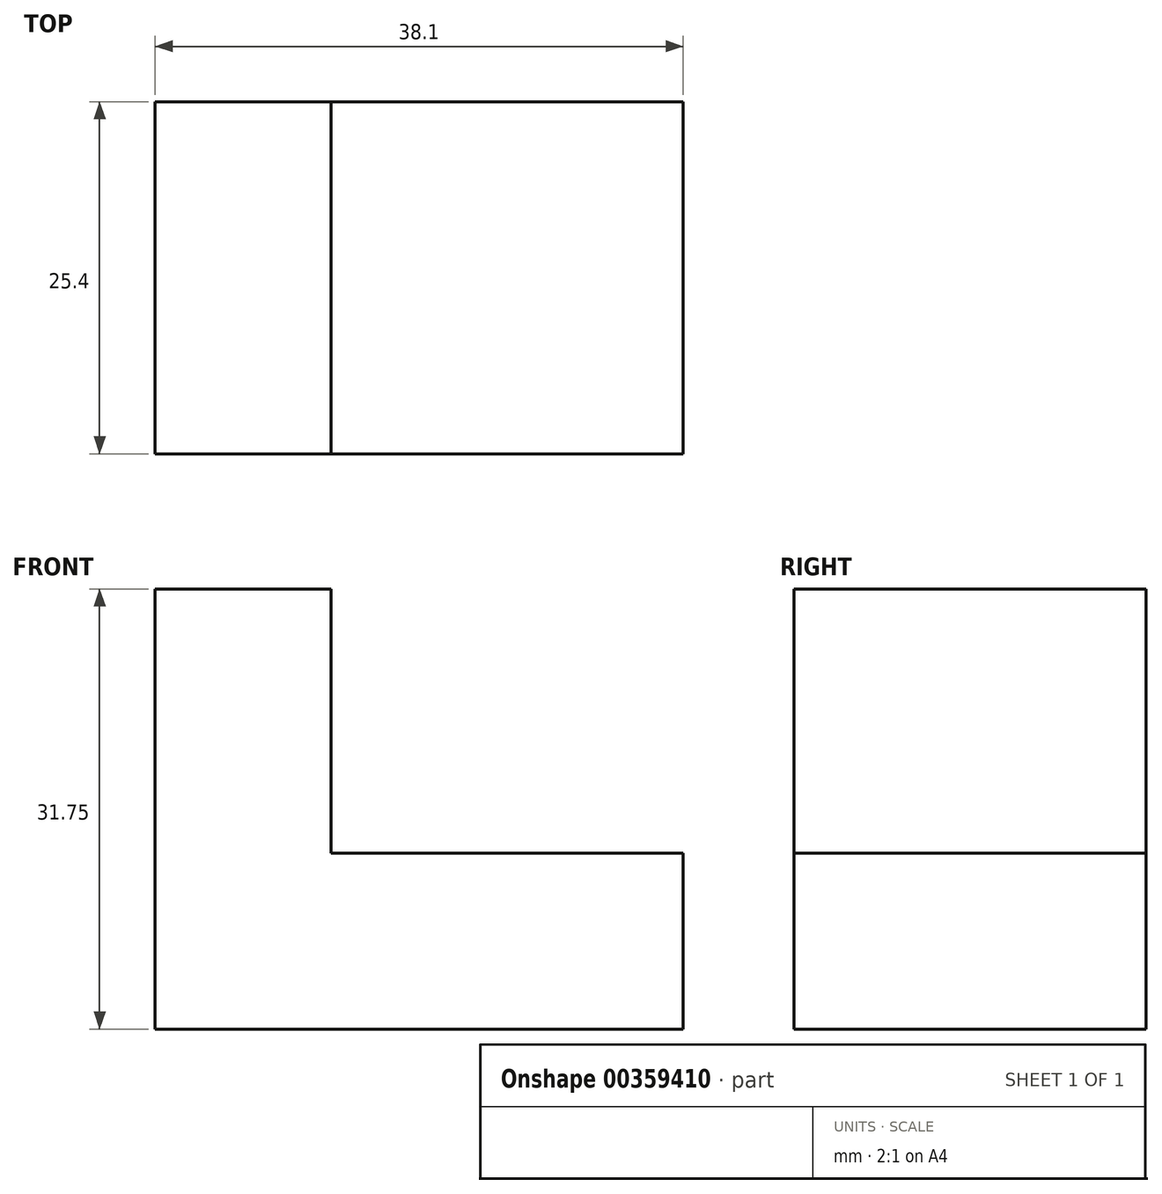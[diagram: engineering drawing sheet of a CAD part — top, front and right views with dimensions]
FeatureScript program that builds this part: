
annotation { "Feature Type Name" : "Feature", "Feature Type Description" : "" }
export const myFeature = defineFeature(function(context is Context, id is Id, definition is map)
    precondition{}
    {
        {
            var Q0;
            Q0=qCreatedBy(makeId("Front.planeOp"),FACE);
            var sketch = newSketch(context, id + "F0", { "sketchPlane" : qUnion([Q0])});
            skLineSegment(sketch, "E0", {"start": v(0, 31.75) * mm, "end": v(0, 0) * mm});
            skLineSegment(sketch, "E1", {"start": v(0, 0) * mm, "end": v(38.1, 0) * mm});
            skLineSegment(sketch, "E2", {"start": v(38.1, 0) * mm, "end": v(38.1, 12.7) * mm});
            skLineSegment(sketch, "E3", {"start": v(38.1, 12.7) * mm, "end": v(12.7, 12.7) * mm});
            skLineSegment(sketch, "E4", {"start": v(12.7, 12.7) * mm, "end": v(12.7, 31.75) * mm});
            skLineSegment(sketch, "E5", {"start": v(0, 31.75) * mm, "end": v(12.7, 31.75) * mm});
            skSolve(sketch);
        }
        {
            var Q0;
            Q0=makeQuery(id+"F0.imprint","IMPRINT",FACE,{"disambiguationData":[TD([[makeQuery(id+"F0.imprint","IMPRINT",EDGE,{"derivedFrom":sQuery(id+"F0.wireOp",EDGE,"E0")}),1.0]])]});
            extrude(context, id + "F1", {"entities" : qUnion([Q0]), "depth" : 25.4 * mm});
        }
    });
